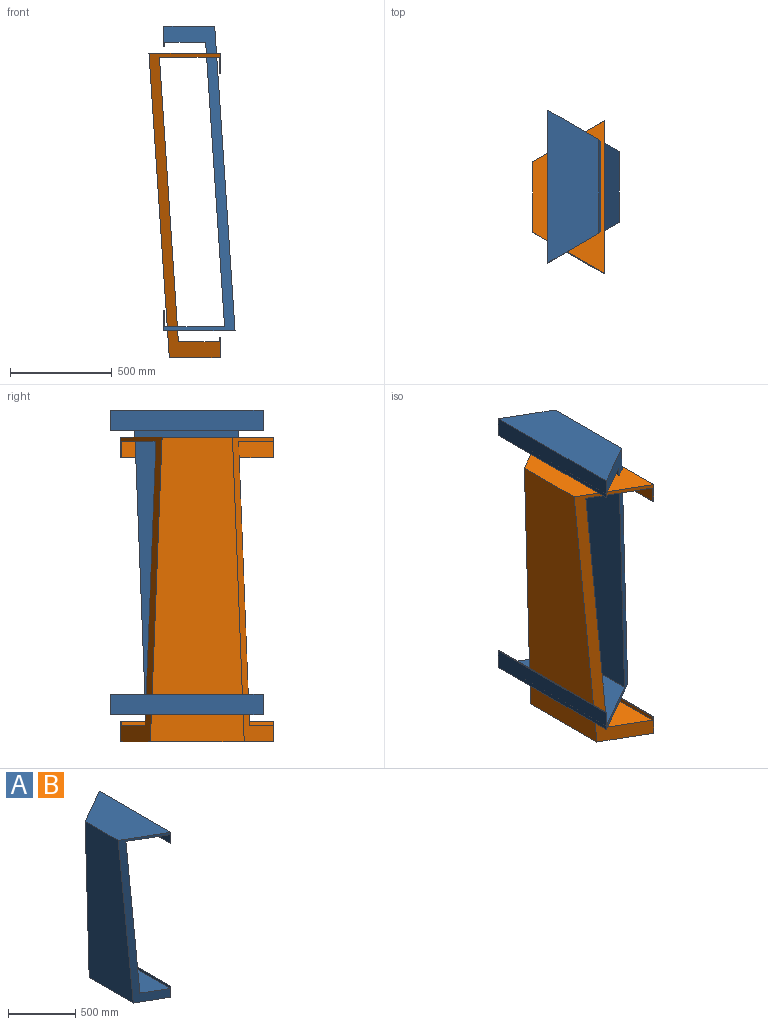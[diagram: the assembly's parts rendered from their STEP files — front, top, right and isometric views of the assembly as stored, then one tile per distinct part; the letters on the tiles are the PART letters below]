
ASSEMBLY  parts=2 mates=1
PART A: 14 faces, bbox 350x750x1496.7 mm
  f0: plane 1496.66x350mm, normal (-0.5,0.87,0), area 112686.4mm2, adj f1,f2,f4,f5,f6,f7,f8,f9
  f1: plane 750x250mm, normal (0,0,-1), area 151415.6mm2, adj f0,f2,f3,f13
  f2: plane 750x100mm, normal (1,0,0), area 75000mm2, adj f0,f1,f3,f12
  f3: plane 1496.66x350mm, normal (-0.5,-0.87,0), area 112686.4mm2, adj f1,f2,f4,f5,f6,f7,f8,f9
  f4: plane 750x350mm, normal (0,0,1), area 191774.6mm2, adj f0,f3,f5,f13
  f5: plane 750x100mm, normal (1,0,0), area 75000mm2, adj f0,f3,f4,f6
  f6: plane 750x4mm, normal (0,0,-1), area 2990.8mm2, adj f0,f3,f5,f7
  f7: plane 745.38x80mm, normal (-1,0,0), area 59630.5mm2, adj f0,f3,f6,f8
  f8: plane 745.38x294.55mm, normal (0,0,-1), area 169462.2mm2, adj f0,f3,f7,f9
  f9: plane 1396.66x513.02mm, normal (1,0,0.07), area 642692.3mm2, adj f0,f3,f8,f10
  f10: plane 745.38x201.23mm, normal (0,0,1), area 126616mm2, adj f0,f3,f9,f11
  f11: plane 745.38x20mm, normal (-1,0,0), area 14907.6mm2, adj f0,f3,f10,f12
  f12: plane 750x4mm, normal (0,0,1), area 2990.8mm2, adj f0,f2,f3,f11
  f13: plane 1496.66x461.33mm, normal (-1,0,-0.07), area 605384.8mm2, adj f0,f1,f3,f4
PART B: same geometry as A
PLACE A rot(axis=(0,-1,0),180deg) t=(1022.33,51.77,1630.18)mm
PLACE B at identity fixed
MATE parallel A.f9 <-> B.f9  axis (-1,0,-0.07) through (622.88,51.77,879.16)mm
